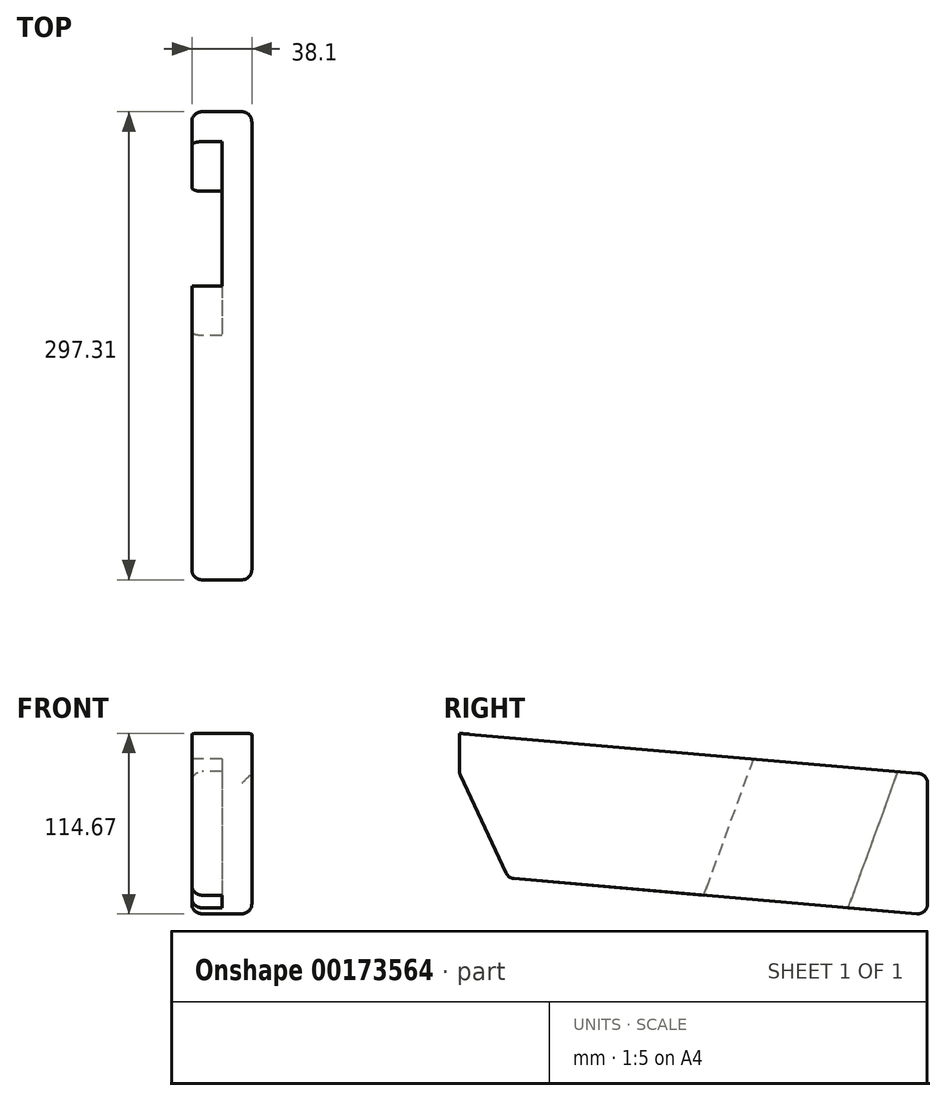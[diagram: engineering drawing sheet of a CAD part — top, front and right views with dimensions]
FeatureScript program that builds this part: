
annotation { "Feature Type Name" : "Feature", "Feature Type Description" : "" }
export const myFeature = defineFeature(function(context is Context, id is Id, definition is map)
    precondition{}
    {
        {
            var Q0;
            Q0=qCreatedBy(makeId("Right.planeOp"),FACE);
            var sketch = newSketch(context, id + "F0", { "sketchPlane" : qUnion([Q0])});
            skLineSegment(sketch, "E0", {"start": v(0, 0) * mm, "end": v(0, -89.24) * mm});
            skLineSegment(sketch, "E1", {"start": v(0, -89.24) * mm, "end": v(-266.28, -65.94) * mm});
            skLineSegment(sketch, "E2", {"start": v(-297.31, 26.01) * mm, "end": v(0, 0) * mm});
            skLineSegment(sketch, "E3", {"start": v(-297.31, 26.01) * mm, "end": v(-297.31, 0.61) * mm});
            skLineSegment(sketch, "E4", {"start": v(-297.31, 0.61) * mm, "end": v(-266.28, -65.94) * mm});
            skSolve(sketch);
        }
        {
            var Q0;
            Q0=makeQuery(id+"F0.imprint","IMPRINT",FACE,{"disambiguationData":[TD([[makeQuery(id+"F0.imprint","IMPRINT",EDGE,{"derivedFrom":sQuery(id+"F0.wireOp",EDGE,"E0")}),-1.0]])]});
            extrude(context, id + "F1", {"entities" : qUnion([Q0]), "depth" : 38.1 * mm});
        }
        {
            var Q0;
            Q0=makeQuery(id+"F1.opExtrude","CAP_FACE",FACE,{"disambiguationData":[OSD([sQuery(id+"F0.wireOp",EDGE,"E0"),sQuery(id+"F0.wireOp",EDGE,"E1"),sQuery(id+"F0.wireOp",EDGE,"E2"),sQuery(id+"F0.wireOp",EDGE,"E3"),sQuery(id+"F0.wireOp",EDGE,"E4")])],"isStart":true});
            var sketch = newSketch(context, id + "F2", { "sketchPlane" : qUnion([Q0])});
            skLineSegment(sketch, "E5", {"start": v(19.02, 1.66) * mm, "end": v(50.5, -84.82) * mm});
            skLineSegment(sketch, "E6.0", {"start": v(110.7, 9.69) * mm, "end": v(142.18, -76.8) * mm});
            skLineSegment(sketch, "E7", {"start": v(50.5, -84.82) * mm, "end": v(142.18, -76.8) * mm});
            skLineSegment(sketch, "E8", {"start": v(19.02, 1.66) * mm, "end": v(110.7, 9.69) * mm});
            skSolve(sketch);
        }
        {
            var Q0;
            Q0 = qSketchRegion(id + "F2", true);
            extrude(context, id + "F3", {"entities" : qUnion([Q0]), "operationType" : NewBodyOperationType.REMOVE, "oppositeDirection" : true, "depth" : 19.05 * mm});
        }
        {
            var Q0;
            Q0=makeQuery(id+"F1.opExtrude","CAP_EDGE",EDGE,{"disambiguationData":[OSD([sQuery(id+"F0.wireOp",EDGE,"E3")])],"isStart":true});
            var Q1;
            Q1=makeQuery(id+"F1.opExtrude","CAP_EDGE",EDGE,{"disambiguationData":[OSD([sQuery(id+"F0.wireOp",EDGE,"E3")])],"isStart":false});
            var Q2;
            Q2=makeQuery(id+"F1.opExtrude","CAP_EDGE",EDGE,{"disambiguationData":[OSD([sQuery(id+"F0.wireOp",EDGE,"E4")])],"isStart":false});
            var Q3;
            Q3=makeQuery(id+"F1.opExtrude","CAP_EDGE",EDGE,{"disambiguationData":[OSD([sQuery(id+"F0.wireOp",EDGE,"E4")])],"isStart":true});
            var Q4;
            Q4=makeQuery(id+"F1.opExtrude","SWEPT_EDGE",EDGE,{"disambiguationData":[OSD([sQuery(id+"F0.wireOp",EDGE,"E1"),sQuery(id+"F0.wireOp",EDGE,"E4")])]});
            var Q5;
            Q5=makeQuery(id+"F1.opExtrude","CAP_EDGE",EDGE,{"disambiguationData":[OSD([sQuery(id+"F0.wireOp",EDGE,"E1")])],"isStart":false});
            var Q6;
            Q6=makeQuery(id+"F1.opExtrude","CAP_EDGE",EDGE,{"disambiguationData":[OSD([sQuery(id+"F0.wireOp",EDGE,"E0")])],"isStart":false});
            var Q7;
            Q7=makeQuery(id+"F1.opExtrude","SWEPT_EDGE",EDGE,{"disambiguationData":[OSD([sQuery(id+"F0.wireOp",EDGE,"E0"),sQuery(id+"F0.wireOp",EDGE,"E2")])]});
            var Q8;
            {var subQ0=sQuery(id+"F0.wireOp",EDGE,"E0");var subQ1=sQuery(id+"F0.wireOp",EDGE,"E1");Q8=makeQuery(id+"F3.boolean.opBoolean","SPLIT",EDGE,{"disambiguationData":[TD([makeQuery(id+"F1.opExtrude","SWEPT_FACE",FACE,{"disambiguationData":[OSD([subQ0])]})])],"derivedFrom":makeQuery(id+"F1.opExtrude","CAP_EDGE",EDGE,{"disambiguationData":[OSD([subQ1])],"isStart":true})});}
            var Q9;
            {var subQ0=sQuery(id+"F0.wireOp",EDGE,"E4");var subQ1=sQuery(id+"F0.wireOp",EDGE,"E1");Q9=makeQuery(id+"F3.boolean.opBoolean","SPLIT",EDGE,{"disambiguationData":[TD([makeQuery(id+"F1.opExtrude","SWEPT_FACE",FACE,{"disambiguationData":[OSD([subQ0])]})])],"derivedFrom":makeQuery(id+"F1.opExtrude","CAP_EDGE",EDGE,{"disambiguationData":[OSD([subQ1])],"isStart":true})});}
            var Q10;
            Q10=makeQuery(id+"F1.opExtrude","SWEPT_EDGE",EDGE,{"disambiguationData":[OSD([sQuery(id+"F0.wireOp",EDGE,"E0"),sQuery(id+"F0.wireOp",EDGE,"E1")])]});
            var Q11;
            Q11=makeQuery(id+"F1.opExtrude","CAP_EDGE",EDGE,{"disambiguationData":[OSD([sQuery(id+"F0.wireOp",EDGE,"E0")])],"isStart":true});
            var Q12;
            {var subQ0=sQuery(id+"F0.wireOp",EDGE,"E0");var subQ1=sQuery(id+"F0.wireOp",EDGE,"E2");Q12=makeQuery(id+"F3.boolean.opBoolean","SPLIT",EDGE,{"disambiguationData":[TD([makeQuery(id+"F1.opExtrude","SWEPT_FACE",FACE,{"disambiguationData":[OSD([subQ0])]})])],"derivedFrom":makeQuery(id+"F1.opExtrude","CAP_EDGE",EDGE,{"disambiguationData":[OSD([subQ1])],"isStart":true})});}
            var Q13;
            Q13=makeQuery(id+"F1.opExtrude","SWEPT_EDGE",EDGE,{"disambiguationData":[OSD([sQuery(id+"F0.wireOp",EDGE,"E3"),sQuery(id+"F0.wireOp",EDGE,"E4")])]});
            fillet(context, id + "F4", {"entities" : qUnion([Q0, Q1, Q2, Q3, Q4, Q5, Q6, Q7, Q8, Q9, Q10, Q11, Q12, Q13]), "radius" : 6.35 * mm, "tangentPropagation" : true, "allowEdgeOverflow" : false});
        }
    });
